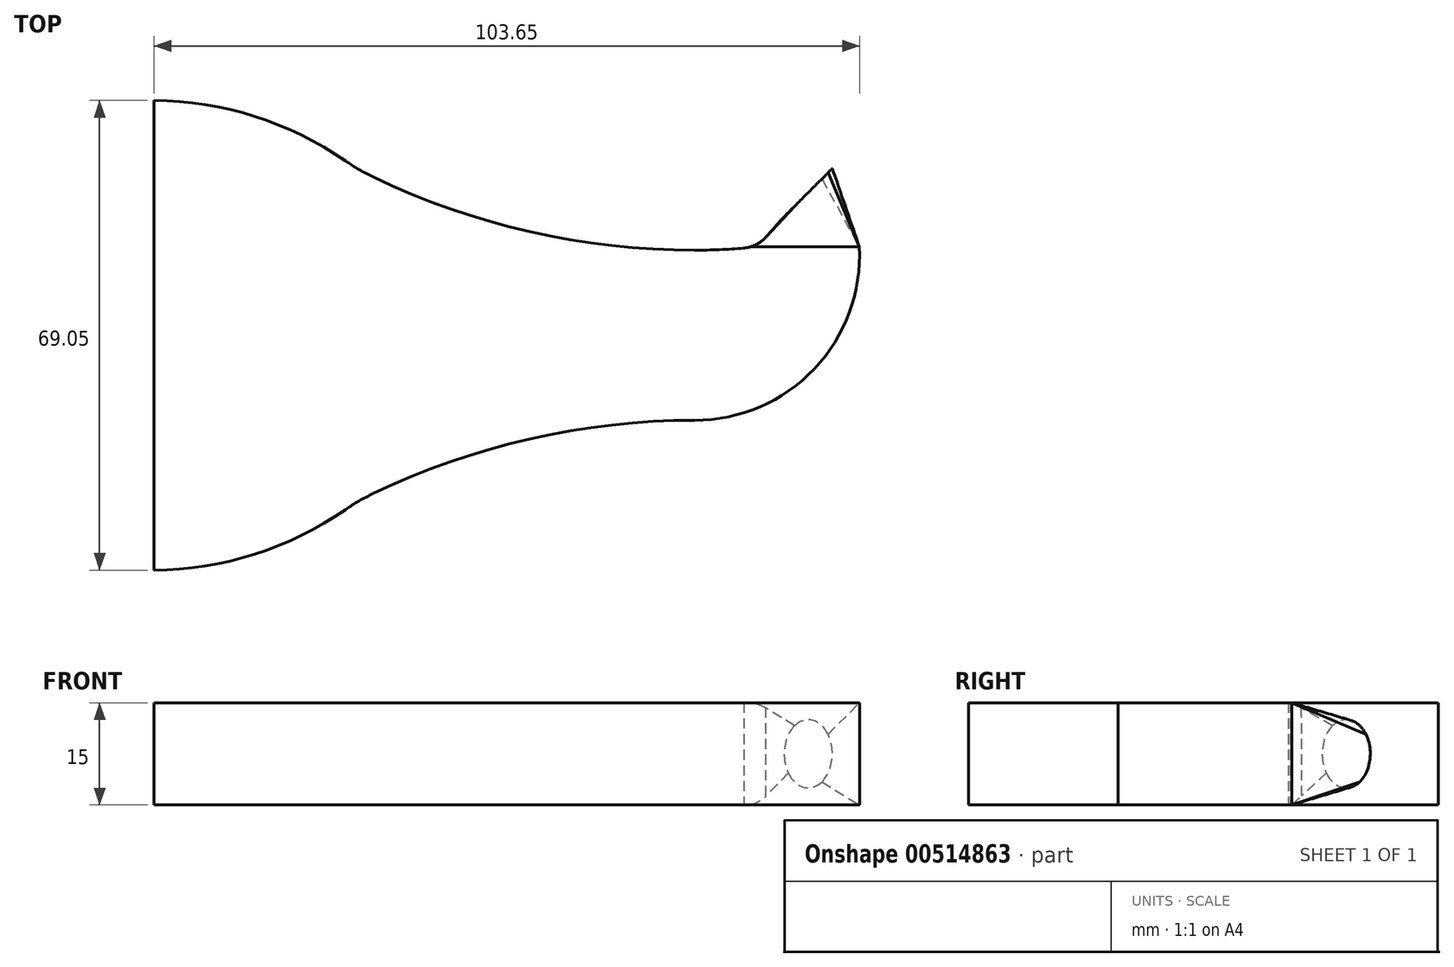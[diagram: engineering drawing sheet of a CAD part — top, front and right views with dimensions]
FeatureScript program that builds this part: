
annotation { "Feature Type Name" : "Feature", "Feature Type Description" : "" }
export const myFeature = defineFeature(function(context is Context, id is Id, definition is map)
    precondition{}
    {
        {
            var Q0;
            Q0=qCreatedBy(makeId("Top.planeOp"),FACE);
            var sketch = newSketch(context, id + "F0", { "sketchPlane" : qUnion([Q0])});
            skLineSegment(sketch, "E0.left", {"start": v(-50, 50) * mm, "end": v(-50, -50) * mm});
            skPoint(sketch, "E0.middle", {"position": v(0, 0) * mm});
            skLineSegment(sketch, "E1", {"start": v(-50, 50) * mm, "end": v(-50, 40) * mm});
            skLineSegment(sketch, "E2", {"start": v(50, 40) * mm, "end": v(42.93, 32.93) * mm});
            skLineSegment(sketch, "E3", {"start": v(42.93, 32.93) * mm, "end": v(46.46, 36.46) * mm});
            skLineSegment(sketch, "E4", {"start": v(-50, 0) * mm, "end": v(-50, -10) * mm});
            skLineSegment(sketch, "E5", {"start": v(-50, -10) * mm, "end": v(-50, 15) * mm});
            skLineSegment(sketch, "E6", {"start": v(-50, 15) * mm, "end": v(114.78, 15) * mm});
            skLineSegment(sketch, "E7", {"start": v(42.93, 32.93) * mm, "end": v(42.93, -37.04) * mm});
            skLineSegment(sketch, "E8", {"start": v(-50, 15) * mm, "end": v(30, 15) * mm});
            skLineSegment(sketch, "E9", {"start": v(30, 15) * mm, "end": v(30, 30) * mm});
            skLineSegment(sketch, "E10", {"start": v(30, 15) * mm, "end": v(30, 0) * mm});
            skLineSegment(sketch, "E11", {"start": v(42.93, 32.93) * mm, "end": v(81, 32.93) * mm});
            skLineSegment(sketch, "E12", {"start": v(46.46, 36.46) * mm, "end": v(46.46, 32.93) * mm});
            skLineSegment(sketch, "E13", {"start": v(46.46, 36.46) * mm, "end": v(46.46, 0) * mm});
            skLineSegment(sketch, "E14", {"start": v(46.46, 36.46) * mm, "end": v(62.14, 20.79) * mm});
            skLineSegment(sketch, "E15", {"start": v(-50, 50) * mm, "end": v(-109.66, 50) * mm});
            skLineSegment(sketch, "E16", {"start": v(-50, 40) * mm, "end": v(-110.5, 40) * mm});
            skLineSegment(sketch, "E17", {"start": v(-50, 15) * mm, "end": v(-113.83, 15) * mm});
            skLineSegment(sketch, "E18", {"start": v(-50, 0) * mm, "end": v(-113, 0) * mm});
            skLineSegment(sketch, "E19", {"start": v(-50, -10) * mm, "end": v(-113, -10) * mm});
            skLineSegment(sketch, "E20", {"start": v(-50, -50) * mm, "end": v(-111.33, -50) * mm});
            skLineSegment(sketch, "E21", {"start": v(30, 30) * mm, "end": v(95.7, 30) * mm});
            skPoint(sketch, "E22", {"position": v(42.93, 30) * mm});
            skPoint(sketch, "E23", {"position": v(46.46, 30) * mm});
            skPoint(sketch, "E24", {"position": v(42.93, 28.5) * mm});
            skLineSegment(sketch, "E25", {"start": v(30, 15) * mm, "end": v(30, 7.5) * mm});
            skLineSegment(sketch, "E26", {"start": v(30, 15) * mm, "end": v(30, 22.5) * mm});
            skLineSegment(sketch, "E27", {"start": v(30, 15) * mm, "end": v(0, 15) * mm});
            skLineSegment(sketch, "E28", {"start": v(-50, 15) * mm, "end": v(-30, 15) * mm});
            skLineSegment(sketch, "E29", {"start": v(-30, 15) * mm, "end": v(-10, 15) * mm});
            skLineSegment(sketch, "E30", {"start": v(-10, 15) * mm, "end": v(10, 15) * mm});
            skLineSegment(sketch, "E31", {"start": v(30, 30) * mm, "end": v(-50, 30) * mm});
            skLineSegment(sketch, "E32", {"start": v(-50, 40) * mm, "end": v(50, 40) * mm});
            skSolve(sketch);
        }
        {
            var Q0;
            Q0=sQuery(id+"F0.wireOp",EDGE,"E2");
            cPlane(context, id + "F1", {"entities" : qUnion([Q0]), "cplaneType" : CPlaneType.LINE_ANGLE, "offset" : 25 * mm, "angle" : 90 * degree, "width" : 150 * mm, "height" : 150 * mm});
        }
        {
            var Q0;
            Q0=qCreatedBy(id+"F1.planeOp",FACE);
            var sketch = newSketch(context, id + "F2", { "sketchPlane" : qUnion([Q0])});
            skCircle(sketch, "E33", {"center": v(58.64, 0) * mm, "radius": 5 * mm});
            skSolve(sketch);
        }
        {
            var Q0;
            Q0=sQuery(id+"F0.wireOp",VERTEX,"E6.start");
            var Q1;
            Q1=qCreatedBy(makeId("Right.planeOp"),FACE);
            cPlane(context, id + "F3", {"entities" : qUnion([Q0, Q1]), "cplaneType" : CPlaneType.PLANE_POINT, "offset" : 25 * mm, "width" : 150 * mm, "height" : 150 * mm});
        }
        {
            var Q0;
            Q0=qCreatedBy(id+"F3.planeOp",FACE);
            var sketch = newSketch(context, id + "F4", { "sketchPlane" : qUnion([Q0])});
            skPoint(sketch, "E34", {"position": v(15, 0) * mm});
            skLineSegment(sketch, "E35", {"start": v(50, 10) * mm, "end": v(-20, 10) * mm});
            skLineSegment(sketch, "E36", {"start": v(50, -10) * mm, "end": v(-20, -10) * mm});
            skLineSegment(sketch, "E37", {"start": v(50, 10) * mm, "end": v(50, -10) * mm});
            skLineSegment(sketch, "E38", {"start": v(-20, 10) * mm, "end": v(-20, -10) * mm});
            skPoint(sketch, "E39", {"position": v(-50, 0) * mm});
            skSolve(sketch);
        }
        {
            var Q0;
            Q0=qCreatedBy(makeId("Front.planeOp"),FACE);
            var Q1;
            Q1=sQuery(id+"F0.wireOp",VERTEX,"E24");
            cPlane(context, id + "F5", {"entities" : qUnion([Q0, Q1]), "cplaneType" : CPlaneType.PLANE_POINT, "offset" : 25 * mm, "width" : 150 * mm, "height" : 150 * mm});
        }
        {
            var Q0;
            Q0=qCreatedBy(id+"F5.planeOp",FACE);
            var sketch = newSketch(context, id + "F6", { "sketchPlane" : qUnion([Q0])});
            skPoint(sketch, "E40", {"position": v(46.46, 0) * mm});
            skLineSegment(sketch, "E41.bottom", {"start": v(38.96, -7.5) * mm, "end": v(53.96, -7.5) * mm});
            skLineSegment(sketch, "E41.top", {"start": v(38.96, 7.5) * mm, "end": v(53.96, 7.5) * mm});
            skLineSegment(sketch, "E41.left", {"start": v(38.96, -7.5) * mm, "end": v(38.96, 7.5) * mm});
            skLineSegment(sketch, "E41.right", {"start": v(53.96, -7.5) * mm, "end": v(53.96, 7.5) * mm});
            skPoint(sketch, "E42", {"position": v(38.96, 0) * mm});
            skPoint(sketch, "E43", {"position": v(53.96, 0) * mm});
            skSolve(sketch);
        }
        {
            var Q0;
            Q0=qCreatedBy(makeId("Top.planeOp"),FACE);
            var Q1;
            Q1=sQuery(id+"F6.wireOp",VERTEX,"E40");
            cPlane(context, id + "F7", {"entities" : qUnion([Q0, Q1]), "cplaneType" : CPlaneType.PLANE_POINT, "offset" : 25 * mm, "width" : 150 * mm, "height" : 150 * mm});
        }
        {
            var Q0;
            Q0=qCreatedBy(id+"F7.planeOp",FACE);
            var sketch = newSketch(context, id + "F8", { "sketchPlane" : qUnion([Q0])});
            skPoint(sketch, "E44", {"position": v(29.78, 27.97) * mm});
            skPoint(sketch, "E45", {"position": v(29.78, 2.97) * mm});
            skLineSegment(sketch, "E46", {"start": v(29.78, 27.97) * mm, "end": v(29.78, 2.97) * mm});
            skLineSegment(sketch, "E47", {"start": v(29.78, 27.97) * mm, "end": v(25.89, 27.97) * mm});
            skLineSegment(sketch, "E48", {"start": v(29.78, 2.97) * mm, "end": v(25.8, 2.97) * mm});
            skPoint(sketch, "E49", {"position": v(29.78, 15.47) * mm});
            skPoint(sketch, "E50", {"position": v(38.96, 28.5) * mm});
            skPoint(sketch, "E51", {"position": v(53.96, 28.5) * mm});
            skArc(sketch, "E52", {"start": v(29.78, 27.97) * mm, "mid": v(34.38, 28.1) * mm, "end": v(38.96, 28.5) * mm});
            skArc(sketch, "E53", {"start": v(29.78, 2.97) * mm, "mid": v(47.36, 10.54) * mm, "end": v(53.96, 28.5) * mm});
            skLineSegment(sketch, "E54", {"start": v(38.96, 28.5) * mm, "end": v(53.96, 28.5) * mm});
            skLineSegment(sketch, "E55", {"start": v(29.78, 15.47) * mm, "end": v(-60.44, 15.47) * mm});
            skSolve(sketch);
        }
        {
            var Q0;
            Q0=qCreatedBy(makeId("Top.planeOp"),FACE);
            var sketch = newSketch(context, id + "F9", { "sketchPlane" : qUnion([Q0])});
            skPoint(sketch, "E56", {"position": v(-49.65, 50) * mm});
            skPoint(sketch, "E57", {"position": v(-49.9, -19.45) * mm});
            skLineSegment(sketch, "E58", {"start": v(-49.65, 50) * mm, "end": v(-56.24, 50) * mm});
            skLineSegment(sketch, "E59", {"start": v(-49.9, -19.45) * mm, "end": v(-57.6, -19.45) * mm});
            skPoint(sketch, "E60", {"position": v(-50, 40) * mm});
            skPoint(sketch, "E61", {"position": v(-50, 15) * mm});
            skPoint(sketch, "E62", {"position": v(-50, 0) * mm});
            skPoint(sketch, "E63", {"position": v(-50, -10) * mm});
            skLineSegment(sketch, "E64", {"start": v(-49.65, 50) * mm, "end": v(-49.9, -19.45) * mm});
            skLineSegment(sketch, "E65", {"start": v(-20, 40) * mm, "end": v(-20, 40) * mm});
            skPoint(sketch, "E66", {"position": v(-50, -50) * mm});
            skLineSegment(sketch, "E67", {"start": v(-50, 15) * mm, "end": v(-49.74, 24.28) * mm});
            skLineSegment(sketch, "E68", {"start": v(-50, 15) * mm, "end": v(-49.8, 6.28) * mm});
            skLineSegment(sketch, "E69", {"start": v(-49.9, -19.45) * mm, "end": v(-49.8, 5.28) * mm});
            skLineSegment(sketch, "E70", {"start": v(-49.65, 50) * mm, "end": v(-49.74, 25.28) * mm});
            skPoint(sketch, "E71", {"position": v(29.78, 2.97) * mm});
            skPoint(sketch, "E72", {"position": v(29.78, 27.97) * mm});
            skLineSegment(sketch, "E73", {"start": v(29.78, 27.97) * mm, "end": v(24.78, 27.97) * mm});
            skLineSegment(sketch, "E74", {"start": v(29.78, 2.97) * mm, "end": v(24.78, 2.97) * mm});
            skArc(sketch, "E75", {"start": v(-20, 40) * mm, "mid": v(4.18, 31.02) * mm, "end": v(29.78, 27.97) * mm});
            skArc(sketch, "E76", {"start": v(-20, 40) * mm, "mid": v(-34.02, 47.38) * mm, "end": v(-49.65, 50) * mm});
            skLineSegment(sketch, "E77", {"start": v(29.78, 27.97) * mm, "end": v(29.78, 2.97) * mm});
            skLineSegment(sketch, "E78", {"start": v(29.78, 15.47) * mm, "end": v(16.82, 15.47) * mm});
            skArc(sketch, "E79.MirrorCS", {"start": v(-20, -9.05) * mm, "mid": v(4.18, -0.08) * mm, "end": v(29.78, 2.97) * mm});
            skArc(sketch, "E80.MirrorCS", {"start": v(-20, -9.05) * mm, "mid": v(-34.02, -16.43) * mm, "end": v(-49.65, -19.05) * mm});
            skLineSegment(sketch, "E81", {"start": v(-49.65, 50) * mm, "end": v(-49.65, -19.05) * mm});
            skSolve(sketch);
        }
        {
            var Q0;
            Q0=qCreatedBy(makeId("Right.planeOp"),FACE);
            var Q1;
            Q1=sQuery(id+"F4.wireOp",VERTEX,"E34");
            cPlane(context, id + "F10", {"entities" : qUnion([Q0, Q1]), "cplaneType" : CPlaneType.PLANE_POINT, "offset" : 25 * mm, "width" : 150 * mm, "height" : 150 * mm});
        }
        {
            var Q0;
            Q0=qCreatedBy(id+"F10.planeOp",FACE);
            var sketch = newSketch(context, id + "F11", { "sketchPlane" : qUnion([Q0])});
            skPoint(sketch, "E82", {"position": v(50, 0) * mm});
            skPoint(sketch, "E83", {"position": v(-50, 0) * mm});
            skPoint(sketch, "E84", {"position": v(0, 0) * mm});
            skLineSegment(sketch, "E85.bottom", {"start": v(50, 50) * mm, "end": v(-50, 50) * mm});
            skLineSegment(sketch, "E85.top", {"start": v(50, -50) * mm, "end": v(-50, -50) * mm});
            skLineSegment(sketch, "E85.left", {"start": v(50, 50) * mm, "end": v(50, -50) * mm});
            skLineSegment(sketch, "E85.right", {"start": v(-50, 50) * mm, "end": v(-50, -50) * mm});
            skLineSegment(sketch, "E86", {"start": v(50, 0) * mm, "end": v(40, 0) * mm});
            skSolve(sketch);
        }
        {
            var Q0;
            Q0=qCreatedBy(id+"F1.planeOp",FACE);
            var Q1;
            Q1=sQuery(id+"F2.wireOp",VERTEX,"E33.center");
            cPlane(context, id + "F12", {"entities" : qUnion([Q0, Q1]), "cplaneType" : CPlaneType.PLANE_POINT, "offset" : 25 * mm, "width" : 150 * mm, "height" : 150 * mm});
        }
        {
            var Q0;
            Q0=qCreatedBy(id+"F12.planeOp",FACE);
            var sketch = newSketch(context, id + "F13", { "sketchPlane" : qUnion([Q0])});
            skCircle(sketch, "E87", {"center": v(58.64, 0) * mm, "radius": 5 * mm});
            skPoint(sketch, "E88", {"position": v(63.64, 0) * mm});
            skSolve(sketch);
        }
        {
            var Q0;
            Q0=sQuery(id+"F11.wireOp",VERTEX,"E82");
            var Q1;
            Q1=qCreatedBy(makeId("Top.planeOp"),FACE);
            cPlane(context, id + "F14", {"entities" : qUnion([Q0, Q1]), "cplaneType" : CPlaneType.PLANE_POINT, "offset" : 25 * mm, "width" : 150 * mm, "height" : 150 * mm});
        }
        {
            var Q0;
            Q0=makeQuery(id+"F2.imprint","IMPRINT",FACE,{"disambiguationData":[TD([[makeQuery(id+"F2.imprint","IMPRINT",EDGE,{"derivedFrom":sQuery(id+"F2.wireOp",EDGE,"E33")}),1.0]])]});
            var Q1;
            Q1=makeQuery(id+"F6.imprint","IMPRINT",FACE,{"disambiguationData":[TD([[makeQuery(id+"F6.imprint","IMPRINT",EDGE,{"derivedFrom":sQuery(id+"F6.wireOp",EDGE,"E41.bottom")}),1.0]])]});
            loft(context, id + "F15", {"sheetProfilesArray" : [{ "sheetProfileEntities" : qUnion([Q0]) }, { "sheetProfileEntities" : qUnion([Q1]) }]});
        }
        {
            var Q0;
            {var subQ1=sQuery(id+"F9.wireOp",EDGE,"E75");Q0=makeQuery(id+"F9.imprint","IMPRINT",FACE,{"disambiguationData":[TD([[makeQuery(id+"F9.imprint","IMPRINT",EDGE,{"derivedFrom":subQ1}),-1.0]])]});}
            extrude(context, id + "F16", {"entities" : qUnion([Q0]), "operationType" : NewBodyOperationType.ADD, "endBound" : BoundingType.SYMMETRIC, "depth" : 15 * mm, "offsetDistance" : 25 * mm});
        }
        {
            var Q0;
            Q0=makeQuery(id+"F8.imprint","IMPRINT",FACE,{"disambiguationData":[TD([[makeQuery(id+"F8.imprint","IMPRINT",EDGE,{"derivedFrom":sQuery(id+"F8.wireOp",EDGE,"E46")}),1.0]])]});
            extrude(context, id + "F17", {"entities" : qUnion([Q0]), "operationType" : NewBodyOperationType.ADD, "endBound" : BoundingType.SYMMETRIC, "depth" : 15 * mm, "offsetDistance" : 25 * mm});
        }
        {
            var Q0;
            Q0=makeQuery(id+"F17.boolean.opBoolean","MERGE",EDGE,{"derivedFrom":[makeQuery(id+"F15.opLoft","MID_CAP_EDGE",EDGE,{"disambiguationData":[OSD([sQuery(id+"F6.wireOp",EDGE,"E41.bottom"),sQuery(id+"F6.wireOp",EDGE,"E41.top"),sQuery(id+"F6.wireOp",EDGE,"E41.left")])],"capPos":1.0}),makeQuery(id+"F17.opExtrude","SWEPT_EDGE",EDGE,{"disambiguationData":[OSD([sQuery(id+"F8.wireOp",EDGE,"E52"),sQuery(id+"F8.wireOp",EDGE,"E54")])]})]});
            fillet(context, id + "F18", {"entities" : qUnion([Q0]), "radius" : 5 * mm, "tangentPropagation" : true, "allowEdgeOverflow" : false});
        }
        {
            var Q0;
            Q0=makeQuery(id+"F16.opExtrude","SWEPT_EDGE",EDGE,{"disambiguationData":[OSD([sQuery(id+"F9.wireOp",EDGE,"E75"),sQuery(id+"F9.wireOp",EDGE,"E76")])]});
            fillet(context, id + "F19", {"entities" : qUnion([Q0]), "radius" : 30 * mm, "tangentPropagation" : true, "allowEdgeOverflow" : false});
        }
        {
            var Q0;
            Q0=makeQuery(id+"F16.opExtrude","SWEPT_EDGE",EDGE,{"disambiguationData":[OSD([sQuery(id+"F9.wireOp",EDGE,"E79.MirrorCS"),sQuery(id+"F9.wireOp",EDGE,"E80.MirrorCS")])]});
            fillet(context, id + "F20", {"entities" : qUnion([Q0]), "radius" : 30 * mm, "tangentPropagation" : true, "allowEdgeOverflow" : false});
        }
    });
